FREECAD ASSEMBLY — COMPONENT RECIPES ("MainAssembly")

This assembly document has 4 components, labeled P0..P3 below (a component is one placed body or linked part). 4 of them carry a construction recipe — the FreeCAD feature program that regenerates the part from scratch, quoted from this document or its linked companion documents; the rest are supplied as boundary geometry only. No exploded tour is included for this assembly.
COMPONENT P0 — recipe-attached ("Link", a linked part whose construction recipe lives in a companion FreeCAD document of the same project; that document's serialized recipe follows).
Construction recipe (the companion document, serialized — sketch geometry with constraints, then the solid features built on it; lengths are millimeters unless a unit is written):

FCSTD DOCUMENT  (FreeCAD 1.2R20251216 (Git shallow))
Label: BasePart
License: All rights reserved
LicenseURL: https://en.wikipedia.org/wiki/All_rights_reserved
objects: Sketcher::SketchObject×6, PartDesign::Pad×5, PartDesign::Body×3, App::Point×3, PartDesign::Pocket×1, PartDesign::Mirrored×1, PartDesign::Chamfer×1
note: 38 computed .brp shape members not serialized (recipe doc carries the construction recipe); baked Part::Feature solids carry a one-line shape summary decoded from their .brp

FEATURE [Sketcher::SketchObject] Sketch
  ArcFitTolerance = 1e-06
  AttachmentSupport = -> [XY_Plane]
  ExternalTypes = [0]
  FullyConstrained = true
  MakeInternals = false
  MapMode = 5
  sketch-geometry (10):
    g0: LineSegment StartX=-50 StartY=15 StartZ=0 EndX=-50 EndY=-15 EndZ=0
    g1: LineSegment StartX=-40 StartY=-25 StartZ=0 EndX=0 EndY=-25 EndZ=0
    g2: LineSegment StartX=0 StartY=-25 StartZ=0 EndX=0 EndY=25 EndZ=0
    g3: LineSegment StartX=0 StartY=25 StartZ=0 EndX=-40 EndY=25 EndZ=0
    g4: ArcOfCircle CenterX=-40 CenterY=15 CenterZ=0 NormalX=0 NormalY=0 NormalZ=1 AngleXU=0 Radius=10 StartAngle=1.5708 EndAngle=3.14159
    g5: GeomPoint [constr] X=-50 Y=25 Z=0
    g6: ArcOfCircle CenterX=-40 CenterY=-15 CenterZ=0 NormalX=0 NormalY=0 NormalZ=1 AngleXU=0 Radius=10 StartAngle=3.14159 EndAngle=4.71239
    g7: GeomPoint [constr] X=-50 Y=-25 Z=0
    g8: Circle CenterX=-40 CenterY=15 CenterZ=0 NormalX=0 NormalY=0 NormalZ=1 AngleXU=0 Radius=5
    g9: Circle CenterX=-40 CenterY=-15 CenterZ=0 NormalX=0 NormalY=0 NormalZ=1 AngleXU=0 Radius=5
  constraints (23):
    c: Coincident(g1,g2)
    c: Coincident(g2,g3)
    c: Vertical(g0)
    c: Vertical(g2)
    c: Horizontal(g1)
    c: Horizontal(g3)
    c: Distance(g5,g2) = 50
    c: Distance(g7,g5) = 50
    c: Symmetric(g2,g1,g-1)
    c: PointOnObject(g5,g0)
    c: PointOnObject(g5,g3)
    c: Tangent(g0,g4) = -1.5708
    c: Tangent(g3,g4) = -1.5708
    c: PointOnObject(g7,g0)
    c: PointOnObject(g7,g1)
    c: Tangent(g0,g6) = -1.5708
    c: Tangent(g1,g6) = -1.5708
    c: Radius(g4) = 10
    c: Equal(g6,g4)
    c: Coincident(g8,g4)
    c: Coincident(g9,g6)
    c: Equal(g8,g9)
    c: Diameter(g8) = 10
FEATURE [PartDesign::Pad] Pad
  Direction = (0,0,1)
  Length = 5
  Length2 = 10
  Profile = -> Sketch
  ReferenceAxis = -> Sketch [N_Axis]
  Refine = true
  SideType = 0
  Suppressed = false
  Type = 0
  Type2 = 0
FEATURE [Sketcher::SketchObject] Sketch001
  ArcFitTolerance = 1e-06
  AttachmentSupport = -> [Pad]
  ExternalGeometry = -> [Pad]
  ExternalTypes = [0]
  FullyConstrained = true
  MakeInternals = false
  MapMode = 5
  Placement = pos=(0,-25,0) rot=(1,0,0;1.5708rad)
  sketch-geometry (4):
    g0: LineSegment StartX=0 StartY=3 StartZ=0 EndX=-24 EndY=3 EndZ=0
    g1: LineSegment StartX=-24 StartY=3 StartZ=0 EndX=-24.8905 EndY=5 EndZ=0
    g2: LineSegment StartX=-24.8905 StartY=5 StartZ=0 EndX=0 EndY=5 EndZ=0
    g3: LineSegment StartX=0 StartY=5 StartZ=0 EndX=0 EndY=3 EndZ=0
  constraints (11):
    c: PointOnObject(g0,g-2)
    c: Horizontal(g0)
    c: Coincident(g0,g1)
    c: PointOnObject(g1,g-3)
    c: Coincident(g1,g2)
    c: Coincident(g2,g-3)
    c: Coincident(g2,g3)
    c: Coincident(g3,g0)
    c: Distance(g3,g3) = 2
    c: DistanceX(g0,g0) = 24
    c: Angle(g0,g1) = 1.98968
FEATURE [PartDesign::Pocket] Pocket
  BaseFeature = -> Pad
  Direction = (0,1,-2e-16)
  Length = 5
  Length2 = 5
  Profile = -> Sketch001
  ReferenceAxis = -> Sketch001 [N_Axis]
  Refine = true
  SideType = 0
  Suppressed = false
  Type = 1
  Type2 = 0
FEATURE [PartDesign::Mirrored] Mirrored
  BaseFeature = -> Pocket
  MirrorPlane = -> YZ_Plane
  Refine = true
  Suppressed = false
  TransformMode = 1
FEATURE [PartDesign::Body] Body  label="Base"
  AllowCompound = false
  Group = -> [Sketch,Pad,Sketch001,Pocket,Mirrored]
  Origin = -> Origin
  Tip = -> Mirrored
FEATURE [Sketcher::SketchObject] Sketch002
  ArcFitTolerance = 1e-06
  AttachmentSupport = -> [XY_Plane001]
  ExternalTypes = [0]
  FullyConstrained = true
  MakeInternals = false
  MapMode = 5
  sketch-geometry (8):
    g0: LineSegment StartX=0 StartY=25 StartZ=0 EndX=-15 EndY=25 EndZ=0
    g1: ArcOfCircle CenterX=-15 CenterY=15 CenterZ=0 NormalX=0 NormalY=0 NormalZ=1 AngleXU=0 Radius=10 StartAngle=1.5708 EndAngle=3.14159
    g2: LineSegment StartX=-25 StartY=15 StartZ=0 EndX=-25 EndY=-15 EndZ=0
    g3: ArcOfCircle CenterX=-15 CenterY=-15 CenterZ=0 NormalX=0 NormalY=0 NormalZ=1 AngleXU=0 Radius=10 StartAngle=3.14159 EndAngle=4.71239
    g4: LineSegment StartX=-15 StartY=-25 StartZ=0 EndX=0 EndY=-25 EndZ=0
    g5: LineSegment StartX=0 StartY=-25 StartZ=0 EndX=0 EndY=25 EndZ=0
    g6: Circle CenterX=-15 CenterY=15 CenterZ=0 NormalX=0 NormalY=0 NormalZ=1 AngleXU=0 Radius=5
    g7: Circle CenterX=-15 CenterY=-15 CenterZ=0 NormalX=0 NormalY=0 NormalZ=1 AngleXU=0 Radius=5
  constraints (19):
    c: PointOnObject(g0,g-2)
    c: Tangent(g0,g1) = -1.5708
    c: Vertical(g2)
    c: Tangent(g2,g3) = -1.5708
    c: Tangent(g3,g4) = -1.5708
    c: Coincident(g4,g5)
    c: Coincident(g5,g0)
    c: Horizontal(g0)
    c: Horizontal(g4)
    c: Tangent(g1,g2) = -1.5708
    c: Coincident(g6,g1)
    c: Coincident(g7,g3)
    c: DistanceX(g1,g0) = 25
    c: DistanceY(g4,g0) = 50
    c: Diameter(g6) = 10
    c: Radius(g1) = 10
    c: Equal(g6,g7)
    c: Equal(g1,g3)
    c: Symmetric(g4,g0,g-1)
FEATURE [PartDesign::Pad] Pad001
  Direction = (0,0,1)
  Length = 5
  Length2 = 10
  Profile = -> Sketch002
  ReferenceAxis = -> Sketch002 [N_Axis]
  Refine = true
  SideType = 0
  Suppressed = false
  Type = 0
  Type2 = 0
FEATURE [Sketcher::SketchObject] Sketch003
  ArcFitTolerance = 1e-06
  AttachmentSupport = -> [Pad001]
  ExternalGeometry = -> [Pad001]
  ExternalTypes = [0]
  FullyConstrained = true
  MakeInternals = false
  MapMode = 5
  Placement = pos=(0,0,0) rot=(0.57735,0.57735,0.57735;2.0944rad)
  sketch-geometry (7):
    g0: LineSegment StartX=-25 StartY=5 StartZ=0 EndX=25 EndY=5 EndZ=0
    g1: ArcOfCircle CenterX=-25 CenterY=20 CenterZ=0 NormalX=0 NormalY=0 NormalZ=1 AngleXU=0 Radius=15 StartAngle=4.71239 EndAngle=6.28319
    g2: ArcOfCircle CenterX=25 CenterY=20 CenterZ=0 NormalX=0 NormalY=0 NormalZ=1 AngleXU=0 Radius=15 StartAngle=3.14159 EndAngle=4.71239
    g3: LineSegment StartX=-10 StartY=20 StartZ=0 EndX=-10 EndY=35 EndZ=0
    g4: LineSegment StartX=10 StartY=20 StartZ=0 EndX=10 EndY=35 EndZ=0
    g5: ArcOfCircle CenterX=0 CenterY=35 CenterZ=0 NormalX=0 NormalY=0 NormalZ=1 AngleXU=0 Radius=10 StartAngle=0 EndAngle=3.14159
    g6: Circle CenterX=0 CenterY=35 CenterZ=0 NormalX=0 NormalY=0 NormalZ=1 AngleXU=0 Radius=2.5
  constraints (15):
    c: Coincident(g0,g-3)
    c: Coincident(g0,g-4)
    c: Vertical(g3)
    c: Vertical(g4)
    c: Tangent(g1,g0) = -1.5708
    c: Tangent(g2,g0) = -1.5708
    c: Tangent(g3,g1) = -1.5708
    c: Tangent(g4,g2) = 1.5708
    c: Tangent(g5,g3) = 1.5708
    c: Tangent(g5,g4) = -1.5708
    c: PointOnObject(g5,g-2)
    c: DistanceY(g0,g5) = 30
    c: Radius(g5) = 10
    c: Diameter(g6) = 5
    c: Coincident(g6,g5)
FEATURE [PartDesign::Pad] Pad002
  BaseFeature = -> Pad001
  Direction = (1,0,0)
  Length = 5
  Length2 = 10
  Profile = -> Sketch003
  ReferenceAxis = -> Sketch003 [N_Axis]
  Refine = true
  Reversed = true
  SideType = 0
  Suppressed = false
  Type = 0
  Type2 = 0
FEATURE [Sketcher::SketchObject] Sketch004
  ArcFitTolerance = 1e-06
  AttachmentSupport = -> [Pad002]
  ExternalGeometry = -> [Pad002]
  ExternalTypes = [0]
  FullyConstrained = true
  MakeInternals = false
  MapMode = 5
  Placement = pos=(-5,0,0) rot=(0.57735,-0.57735,-0.57735;2.0944rad)
  sketch-geometry (4):
    g0: LineSegment StartX=-2.5 StartY=25 StartZ=0 EndX=-2.5 EndY=5 EndZ=0
    g1: LineSegment StartX=-2.5 StartY=5 StartZ=0 EndX=2.5 EndY=5 EndZ=0
    g2: LineSegment StartX=2.5 StartY=5 StartZ=0 EndX=2.5 EndY=25 EndZ=0
    g3: LineSegment StartX=2.5 StartY=25 StartZ=0 EndX=-2.5 EndY=25 EndZ=0
  constraints (11):
    c: Coincident(g0,g1)
    c: Coincident(g1,g2)
    c: Coincident(g2,g3)
    c: Coincident(g3,g0)
    c: Vertical(g0)
    c: Vertical(g2)
    c: Horizontal(g1)
    c: PointOnObject(g1,g-3)
    c: Symmetric(g0,g2,g-2)
    c: Distance(g3,g3) = 5
    c: DistanceY(g2,g2) = 20
FEATURE [PartDesign::Pad] Pad003
  BaseFeature = -> Pad002
  Direction = (-1,0,0)
  Length = 20
  Length2 = 10
  Profile = -> Sketch004
  ReferenceAxis = -> Sketch004 [N_Axis]
  Refine = true
  SideType = 0
  Suppressed = false
  Type = 0
  Type2 = 0
FEATURE [PartDesign::Chamfer] Chamfer
  Angle = 45
  Base = -> Pad003 [Edge54]
  BaseFeature = -> Pad003
  ChamferType = 0
  FlipDirection = false
  Refine = true
  Size = 19.99
  Size2 = 1
  SupportTransform = false
  Suppressed = false
  UseAllEdges = false
FEATURE [PartDesign::Body] Body001  label="Bracket"
  AllowCompound = false
  Group = -> [Sketch002,Pad001,Sketch003,Pad002,Sketch004,Pad003,Chamfer]
  Origin = -> Origin001
  Placement = pos=(0,62.122,0) rot=(0,0,1;0rad)
  Tip = -> Chamfer
FEATURE [App::Point] Origin002  label="Origin"
  Role = Origin
FEATURE [App::Point] Origin003  label="Origin"
  Role = Origin
FEATURE [App::Point] Origin005
  Role = Origin
FEATURE [Sketcher::SketchObject] Sketch005
  ArcFitTolerance = 1e-06
  AttachmentSupport = -> [Origin004]
  ExternalTypes = [0]
  FullyConstrained = true
  MakeInternals = false
  MapMode = 5
  sketch-geometry (6):
    g0: ArcOfCircle CenterX=0 CenterY=0 CenterZ=0 NormalX=0 NormalY=0 NormalZ=1 AngleXU=0 Radius=8 StartAngle=1.5708 EndAngle=4.71239
    g1: ArcOfCircle CenterX=100 CenterY=0 CenterZ=0 NormalX=0 NormalY=0 NormalZ=1 AngleXU=0 Radius=8 StartAngle=4.71239 EndAngle=7.85398
    g2: LineSegment StartX=-1.114e-13 StartY=8 StartZ=0 EndX=100 EndY=8 EndZ=0
    g3: LineSegment StartX=-1.081e-13 StartY=-8 StartZ=0 EndX=100 EndY=-8 EndZ=0
    g4: Circle CenterX=0 CenterY=0 CenterZ=0 NormalX=0 NormalY=0 NormalZ=1 AngleXU=0 Radius=2.5
    g5: Circle CenterX=100 CenterY=0 CenterZ=0 NormalX=0 NormalY=0 NormalZ=1 AngleXU=0 Radius=2.5
  constraints (13):
    c: Tangent(g0,g2) = 1.5708
    c: Tangent(g0,g3) = -1.5708
    c: Tangent(g1,g2) = 1.5708
    c: Tangent(g1,g3) = -1.5708
    c: Equal(g0,g1)
    c: Radius(g0) = 8
    c: Coincident(g0,g-1)
    c: PointOnObject(g1,g-1)
    c: Coincident(g4,g0)
    c: Coincident(g5,g1)
    c: Diameter(g4) = 5
    c: Equal(g4,g5)
    c: DistanceX(g0,g1) = 100
FEATURE [PartDesign::Pad] Pad004
  Direction = (0,0,1)
  Length = 2
  Length2 = 10
  Profile = -> Sketch005
  ReferenceAxis = -> Sketch005 [N_Axis]
  Refine = true
  SideType = 0
  Suppressed = false
  Type = 0
  Type2 = 0
FEATURE [PartDesign::Body] Body002  label="Link"
  AllowCompound = true
  Group = -> [Sketch005,Pad004]
  Origin = -> Origin004
  Placement = pos=(0,86.082,0) rot=(0,0,1;0rad)
  Tip = -> Pad004
COMPONENT P1 — same part as P0; its construction recipe is shown at P0.
COMPONENT P2 — same part as P0; its construction recipe is shown at P0.
COMPONENT P3 — same part as P0; its construction recipe is shown at P0.
PROVENANCE & LICENSES
A FreeCAD (.FCStd) document from a public repository crawl; recipes are the document's own serialized feature recipes (and, for linked parts, companion documents' recipes).
License: as declared in the source repository (recorded in the dataset sidecar).
